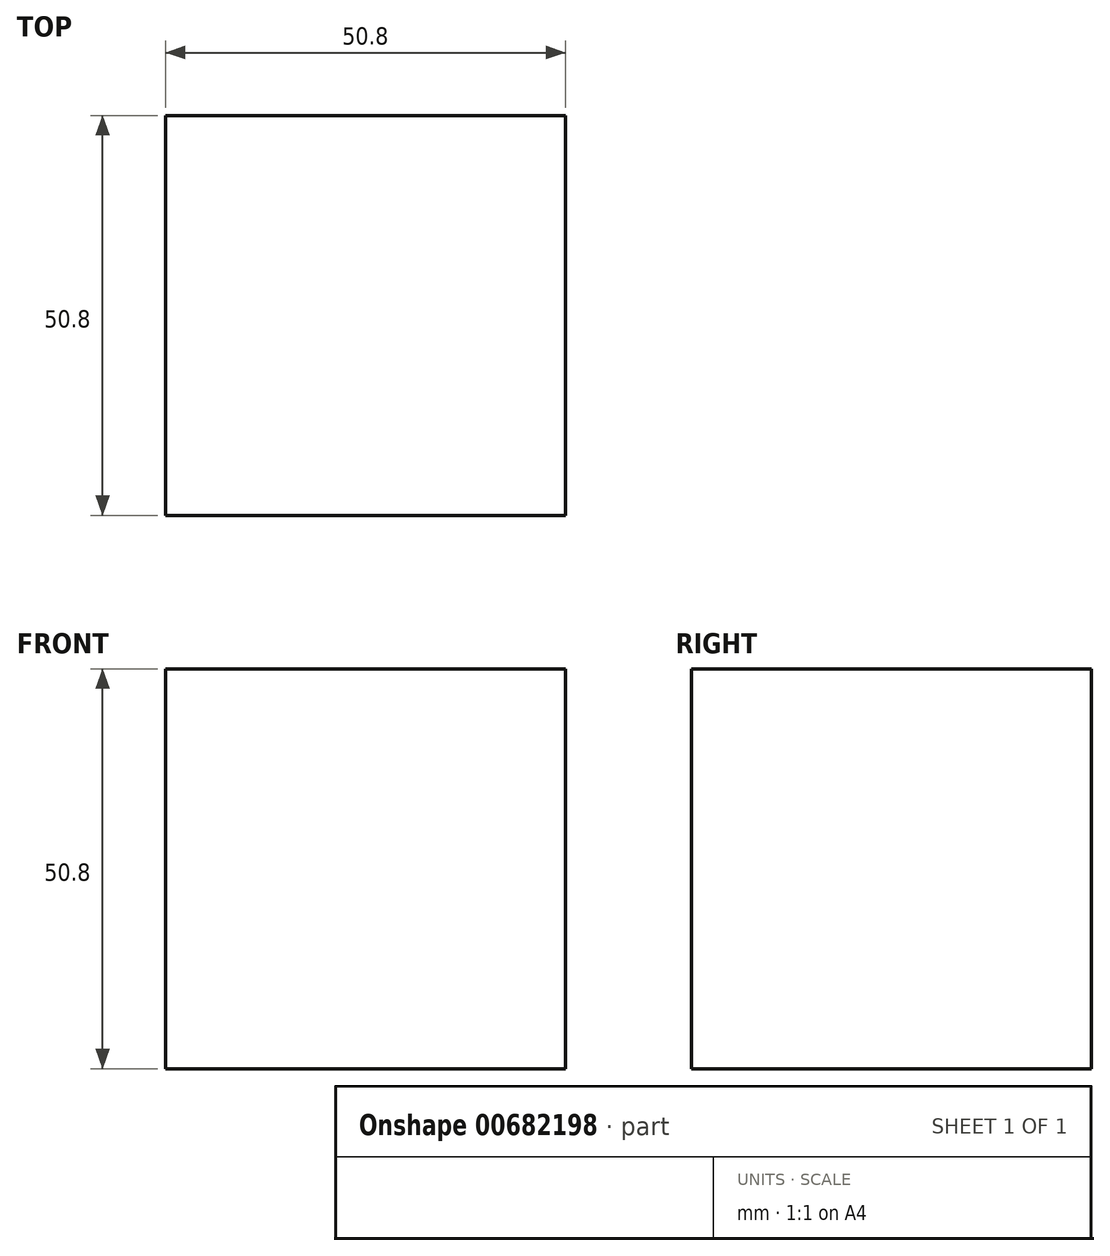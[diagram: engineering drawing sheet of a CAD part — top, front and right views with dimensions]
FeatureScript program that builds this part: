
annotation { "Feature Type Name" : "Feature", "Feature Type Description" : "" }
export const myFeature = defineFeature(function(context is Context, id is Id, definition is map)
    precondition{}
    {
        {
            var Q0;
            Q0=qCreatedBy(makeId("Front.planeOp"),FACE);
            var sketch = newSketch(context, id + "F0", { "sketchPlane" : qUnion([Q0])});
            skLineSegment(sketch, "E0.bottom", {"start": v(9.26, 33.33) * mm, "end": v(60.06, 33.33) * mm});
            skLineSegment(sketch, "E0.top", {"start": v(9.26, -17.47) * mm, "end": v(60.06, -17.47) * mm});
            skLineSegment(sketch, "E0.left", {"start": v(9.26, 33.33) * mm, "end": v(9.26, -17.47) * mm});
            skLineSegment(sketch, "E0.right", {"start": v(60.06, 33.33) * mm, "end": v(60.06, -17.47) * mm});
            skSolve(sketch);
        }
        {
            var Q0;
            Q0 = qSketchRegion(id + "F0", true);
            extrude(context, id + "F1", {"entities" : qUnion([Q0]), "depth" : 50.8 * mm, "offsetDistance" : 25.4 * mm});
        }
        {
            var Q0;
            Q0=qCreatedBy(makeId("Front.planeOp"),FACE);
            var sketch = newSketch(context, id + "F2", { "sketchPlane" : qUnion([Q0])});
            skLineSegment(sketch, "E1.bottom", {"start": v(60.38, 33.33) * mm, "end": v(26.96, 33.33) * mm});
            skLineSegment(sketch, "E1.top", {"start": v(60.38, 6.59) * mm, "end": v(26.96, 6.59) * mm});
            skLineSegment(sketch, "E1.left", {"start": v(60.38, 33.33) * mm, "end": v(60.38, 6.59) * mm});
            skLineSegment(sketch, "E1.right", {"start": v(26.96, 33.33) * mm, "end": v(26.96, 6.59) * mm});
            skSolve(sketch);
        }
        {
            var Q0;
            Q0 = qSketchRegion(id + "F2", true);
            extrude(context, id + "F3", {"entities" : qUnion([Q0]), "operationType" : NewBodyOperationType.REMOVE, "oppositeDirection" : true, "depth" : 25.4 * mm, "offsetDistance" : 25.4 * mm});
        }
    });
